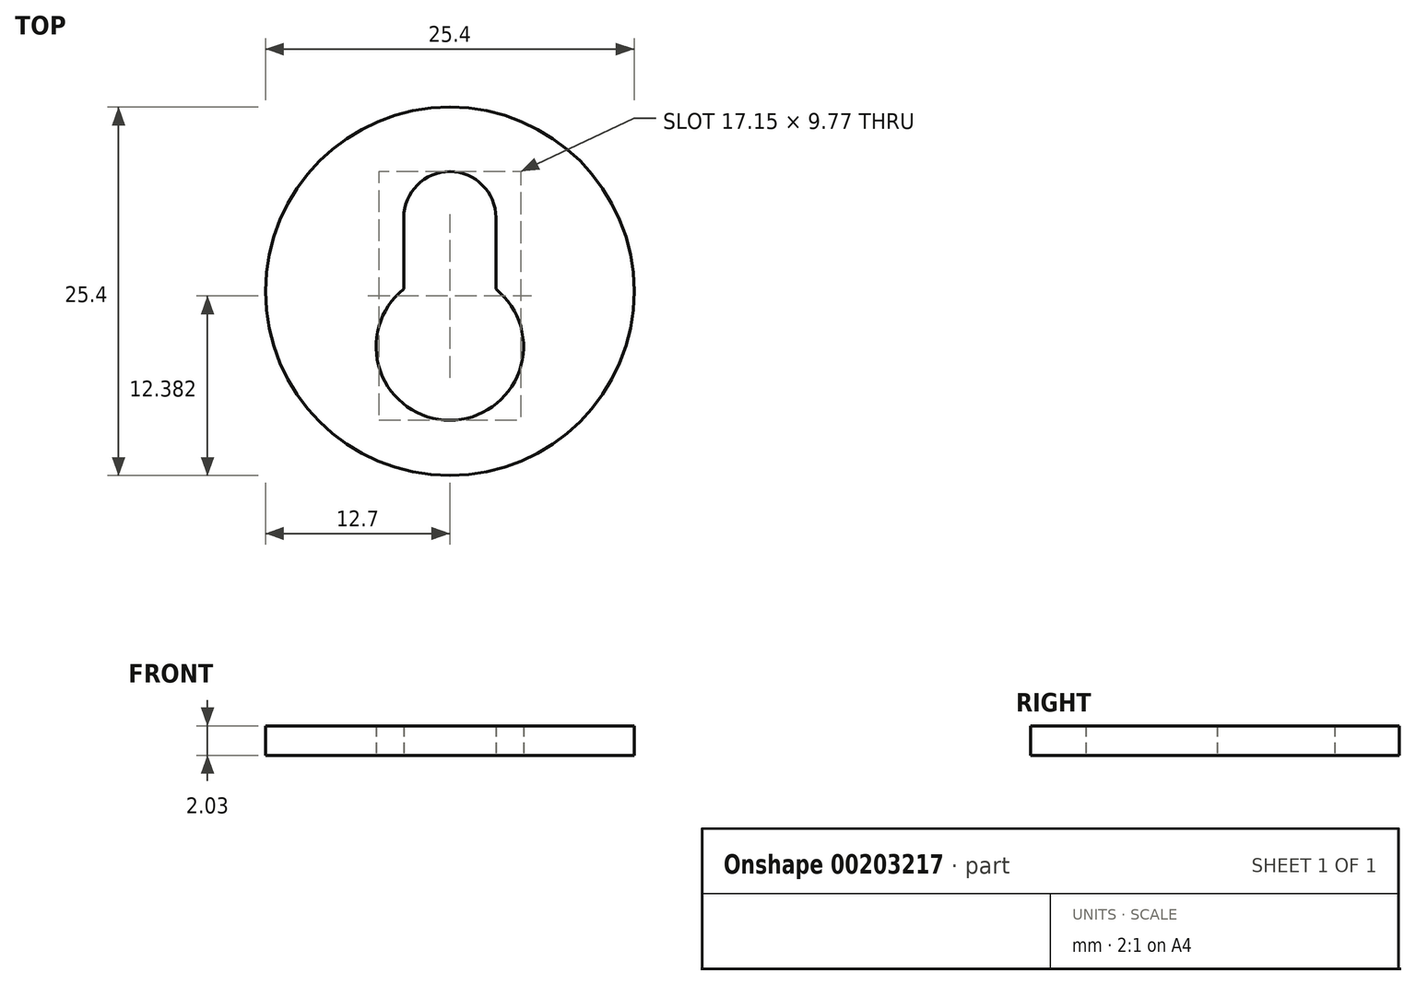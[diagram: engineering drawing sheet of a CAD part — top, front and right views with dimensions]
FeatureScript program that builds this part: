
annotation { "Feature Type Name" : "Feature", "Feature Type Description" : "" }
export const myFeature = defineFeature(function(context is Context, id is Id, definition is map)
    precondition{}
    {
        {
            var Q0;
            Q0=qCreatedBy(makeId("Top.planeOp"),FACE);
            var sketch = newSketch(context, id + "F0", { "sketchPlane" : qUnion([Q0])});
            skCircle(sketch, "E0", {"center": v(0, 0) * mm, "radius": 12.7 * mm});
            skCircle(sketch, "E1", {"center": v(0, -3.81) * mm, "radius": 5.08 * mm});
            skCircle(sketch, "E2", {"center": v(0, 5.08) * mm, "radius": 3.18 * mm});
            skLineSegment(sketch, "E3", {"start": v(-3.18, 5.08) * mm, "end": v(-3.17, 0.16) * mm});
            skLineSegment(sketch, "E4", {"start": v(3.18, 5.08) * mm, "end": v(3.18, 0.16) * mm});
            skSolve(sketch);
        }
        {
            var Q0;
            Q0 = qSketchRegion(id + "F0", true);
            extrude(context, id + "F1", {"entities" : qUnion([Q0]), "depth" : 2.03 * mm});
        }
    });
